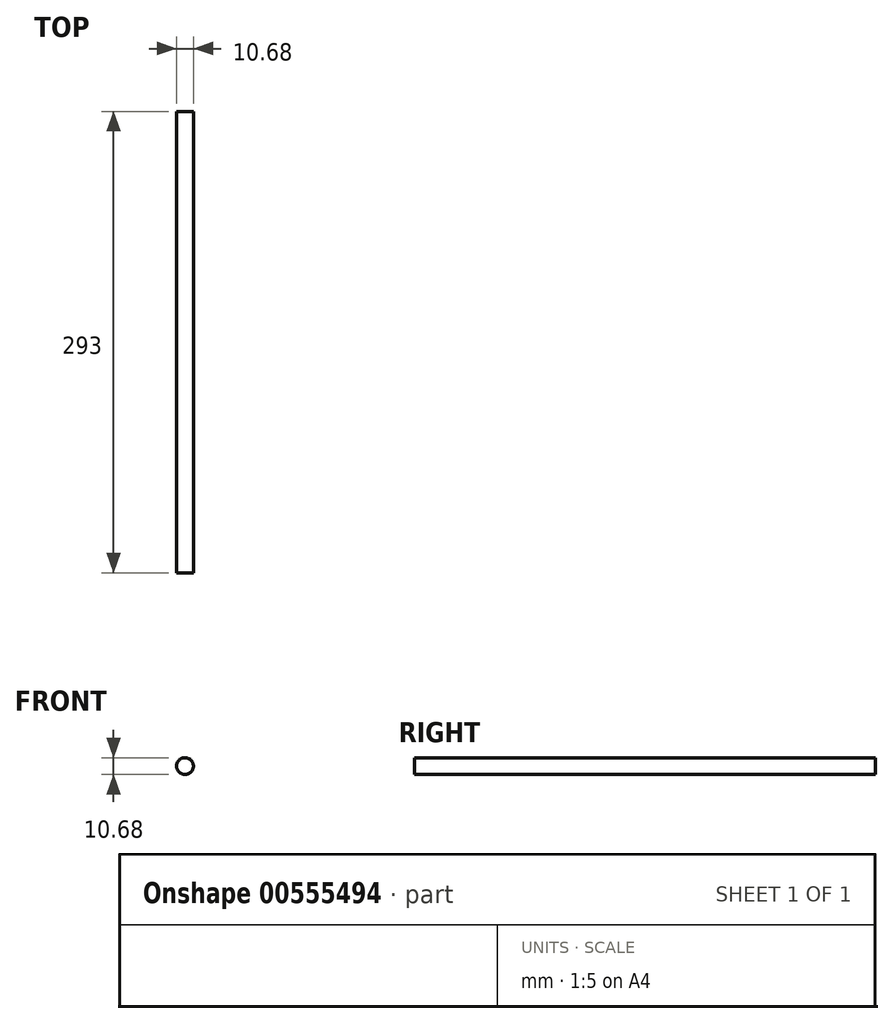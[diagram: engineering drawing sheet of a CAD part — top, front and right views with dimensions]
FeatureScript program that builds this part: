
annotation { "Feature Type Name" : "Feature", "Feature Type Description" : "" }
export const myFeature = defineFeature(function(context is Context, id is Id, definition is map)
    precondition{}
    {
        {
            var Q0;
            Q0=qCreatedBy(makeId("Front.planeOp"),FACE);
            var sketch = newSketch(context, id + "F0", { "sketchPlane" : qUnion([Q0])});
            skCircle(sketch, "E0", {"center": v(0, 0) * mm, "radius": 5.34 * mm});
            skSolve(sketch);
        }
        {
            var Q0;
            Q0 = qSketchRegion(id + "F0", true);
            extrude(context, id + "F1", {"entities" : qUnion([Q0]), "depth" : 293 * mm, "offsetDistance" : 25 * mm});
        }
    });
